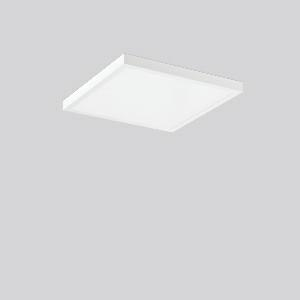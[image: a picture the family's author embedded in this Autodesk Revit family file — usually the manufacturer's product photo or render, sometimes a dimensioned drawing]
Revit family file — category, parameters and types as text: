
# Revit family: sidelite_eco_312377_002_76_e3cb
name_source: partatom
category: Lighting Fixtures
units: mm (PartAtom-declared; Revit-internal decimal feet)

## family parameters
Cut with Voids When Loaded = No
Host = Face
Light Source = No
Part Type = Normal
Room Calculation Point = No
Round Connector Dimension = Use Diameter
Shared = No

## types (1)
- MultiLumen 1 (1 x LED Modul 830, 3400 lm, 3000)
    Apparent Load = 29 VA
    CIE Flux Codes = 63 88 97 100 100
    Color Rendering = 80
    Color Temperature = 3000
    Default Elevation = 1800 mm
    Description = Series: SIDELITE ECO
Highly economical surface mounted luminaire with progressive LED technology. Luminaire frame: aluminium, powder-coated. Mounting frame: sheet steel, powder-coated. Diffuser plastic microprismatic. Lightguide and diffuser made of non-yellowing plastic (PMMA). Lateral light emission (RZB SIDELITE technology) for homogeneous light distribution. Driver integrated. MultiLumen: 4 steps adjustable luminous flux. Factory setting is the lowest offered step. Perfect for office areas (RUG < 19) and environments with computer screens in accordance with EN 12464-1. Qualified for use in the food and drink industry. 
Colour: white
Length: 602 mm
Width: 602 mm
Height: 47 mm
Lamp: LED
Socket: without socket
Colour temperature: 3000K
Colour rendering index (CRI): 80
System power: 29 W
Rated luminous flux: 3400 lm
Luminous efficiency: 117 lm/W
System power 2: 33 W
Rated luminous flux 2: 3750 lm
Luminous efficiency 2: 114 lm/W
System power 3: 35 W
Rated luminous flux 3: 3950 lm
Luminous efficiency 3: 113 lm/W
System power 4: 38 W
Rated luminous flux 4: 4300 lm
Luminous efficiency 4: 113 lm/W
Control gear: Converter, dimmable, DALI
Protection class: II
Type of protection: IP 40
    Height = 47 mm
    Lamp = 1 x LED Modul 830
    Lamp Light Flux = 3400 lm
    Lamp count = 1
    Length = 602 mm
    Lifetime = 50000 h
    Luminous efficacy = 117 lm/W
    Manufacturer = RZB
    ModVariant = No
    Model = 312377.002.76
    Mounting Place = Ceiling
    Mounting Type = Surface mounted
    Number of Poles = 1
    OnlyDefault = Yes
    Power Factor = 1
    Product Name = SIDELITE ECO
    Product group = Surface mounted modular luminaires
    ProductGroupID = 306
    Protection Class = Protection class II
    Protection Degree = IP 40
    RLX_Detail_Level = 1
    RLX_Emergency_Light_Flux = 0 lm
    RLX_Emergency_Type = 0
    RLX_Emergency_Type_DB = No
    RlxData = <blob elided: 22017 chars, md5=76629e2c>
    Socket = socket
    Standby Power = 0 W
    System Light Flux = 3400 lm
    System Power = 29 W
    Type Comments = MultiLumen 1
    Type Image = 312377.002.jpg
    URL = http://relux.com
    VarID = multilumen_1
    Voltage = 230 V
    Voltage Range = 220-240 V
    Weight = 0.00 kg
    Width = 602 mm

## geometry (parser evidence)
native form markers: Blend x4, Sweep x11
no freeform markers — native parametric forms only
